# Revit family: S-800 (DSA)
name_source: partatom
category: Generic Models
revit_build: Autodesk Revit Architecture 2015 (Build: 20141119_1515(x64)
units: mm (PartAtom-declared; Revit-internal decimal feet)

## types (9) — shared parameters
Description = Foam Dock Seal
FollowerCurtain = 3' - 0"
Manufacturer = Entrematic
PadPosition = 1' - 0"
Projection = 0' - 10"
URL = https://www.entrematic.us

## per-type parameters (varying)
| type | DropCurtain | Model | Opening | SidePadHeight | Width |
| 8'x10' Door | 2' - 0" | S-600/DSS | 7' - 6" | 11' - 6" | 9' - 6" |
| 8.5'x10' Door | 2' - 0" | S-600/DSS | 7' - 8" | 11' - 6" | 10' - 0" |
| 9'x10' Door | 1' - 6" | S-600/DSS | 7' - 10" | 11' - 6" | 10' - 7" |
| 8'x9' Door | 2' - 0" | S-600/DSS | 7' - 6" | 10' - 6" | 9' - 6" |
| 8.5'x9' Door | 20' - 0" | S-600/DSS | 7' - 8" | 10' - 6" | 10' - 0" |
| 9'x9' Door | 2' - 0" | S-700/DSH | 7' - 10" | 10' - 6" | 10' - 7" |
| 8.5'x8' Door | 2' - 0" | S-600/DSS | 7' - 8" | 9' - 6" | 10' - 0" |
| 8'x8' Door | 2' - 0" | S-600/DSS | 7' - 6" | 9' - 6" | 9' - 6" |
| 9'x8' Door | 2' - 0" | S-700/DSH | 7' - 10" | 9' - 6" | 10' - 7" |

## geometry (parser evidence)
native form markers: Sweep x2
no freeform markers — native parametric forms only
